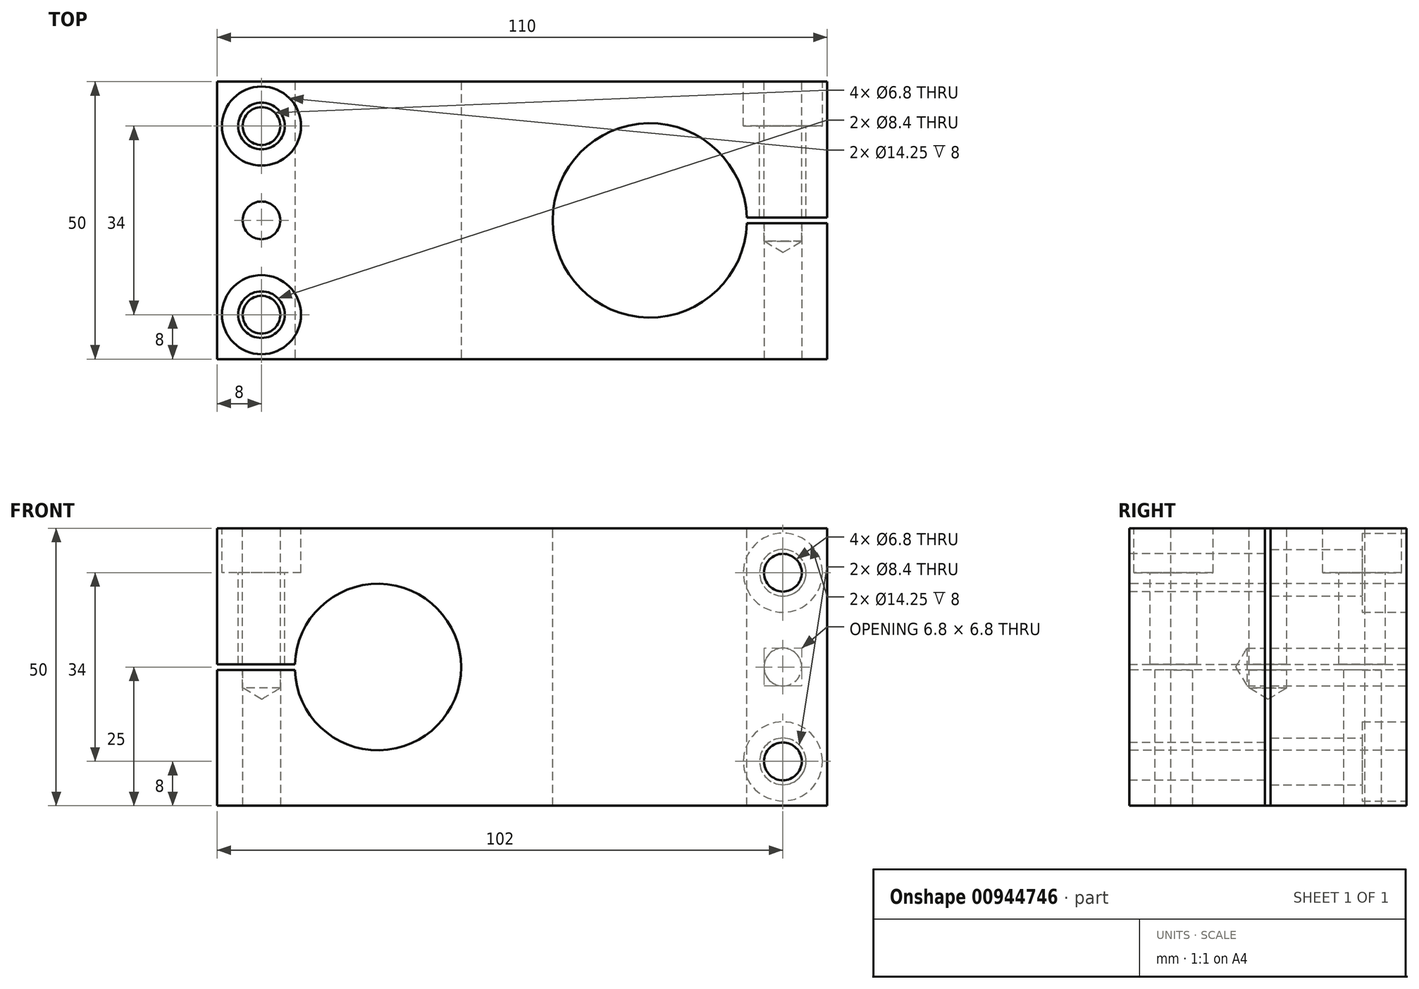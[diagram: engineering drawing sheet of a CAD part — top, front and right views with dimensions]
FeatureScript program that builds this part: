
annotation { "Feature Type Name" : "Feature", "Feature Type Description" : "" }
export const myFeature = defineFeature(function(context is Context, id is Id, definition is map)
    precondition{}
    {
        {
            var Q0;
            Q0=qCreatedBy(makeId("Top.planeOp"),FACE);
            var sketch = newSketch(context, id + "F0", { "sketchPlane" : qUnion([Q0])});
            skLineSegment(sketch, "E0.bottom", {"start": v(-55, 25) * mm, "end": v(55, 25) * mm});
            skLineSegment(sketch, "E0.top", {"start": v(-55, -25) * mm, "end": v(55, -25) * mm});
            skLineSegment(sketch, "E0.left", {"start": v(-55, 25) * mm, "end": v(-55, -25) * mm});
            skLineSegment(sketch, "E0.right", {"start": v(55, 25) * mm, "end": v(55, -25) * mm});
            skPoint(sketch, "E0.middle", {"position": v(0, 0) * mm});
            skSolve(sketch);
        }
        {
            var Q0;
            Q0 = qSketchRegion(id + "F0", true);
            extrude(context, id + "F1", {"entities" : qUnion([Q0]), "endBound" : BoundingType.SYMMETRIC, "depth" : 50 * mm, "offsetDistance" : 25 * mm});
        }
        {
            var Q0;
            Q0=makeQuery(id+"F1.opExtrude","SWEPT_FACE",FACE,{"disambiguationData":[OSD([sQuery(id+"F0.wireOp",EDGE,"E0.top")])]});
            var sketch = newSketch(context, id + "F2", { "sketchPlane" : qUnion([Q0])});
            skPoint(sketch, "E1", {"position": v(-26, 0) * mm});
            skPoint(sketch, "E2", {"position": v(47, -17) * mm});
            skPoint(sketch, "E3", {"position": v(47, 17) * mm});
            skPoint(sketch, "E4", {"position": v(47, 0) * mm});
            skSolve(sketch);
        }
        {
            var Q0;
            Q0=makeQuery(id+"F1.opExtrude","CAP_FACE",FACE,{"disambiguationData":[OSD([sQuery(id+"F0.wireOp",EDGE,"E0.bottom"),sQuery(id+"F0.wireOp",EDGE,"E0.top"),sQuery(id+"F0.wireOp",EDGE,"E0.left"),sQuery(id+"F0.wireOp",EDGE,"E0.right")])],"isStart":false});
            var sketch = newSketch(context, id + "F3", { "sketchPlane" : qUnion([Q0])});
            skPoint(sketch, "E5", {"position": v(23, 0) * mm});
            skPoint(sketch, "E6", {"position": v(-47, 17) * mm});
            skPoint(sketch, "E7", {"position": v(-47, -17) * mm});
            skPoint(sketch, "E8", {"position": v(-47, 0) * mm});
            skSolve(sketch);
        }
        {
            var Q0;
            Q0=makeQuery(id+"F1.opExtrude","CAP_FACE",FACE,{"disambiguationData":[OSD([sQuery(id+"F0.wireOp",EDGE,"E0.bottom"),sQuery(id+"F0.wireOp",EDGE,"E0.top"),sQuery(id+"F0.wireOp",EDGE,"E0.left"),sQuery(id+"F0.wireOp",EDGE,"E0.right")])],"isStart":true});
            var sketch = newSketch(context, id + "F4", { "sketchPlane" : qUnion([Q0])});
            skPoint(sketch, "E9", {"position": v(-47, -17) * mm});
            skPoint(sketch, "E10", {"position": v(-47, 17) * mm});
            skPoint(sketch, "E11", {"position": v(-47, 0) * mm});
            skSolve(sketch);
        }
        {
            var Q0;
            Q0=makeQuery(id+"F1.opExtrude","SWEPT_FACE",FACE,{"disambiguationData":[OSD([sQuery(id+"F0.wireOp",EDGE,"E0.bottom")])]});
            var sketch = newSketch(context, id + "F5", { "sketchPlane" : qUnion([Q0])});
            skPoint(sketch, "E12", {"position": v(-47, 17) * mm});
            skPoint(sketch, "E13", {"position": v(-47, -17) * mm});
            skPoint(sketch, "E14", {"position": v(-47, 0) * mm});
            skSolve(sketch);
        }
        {
            var Q0;
            Q0=sQuery(id+"F2.wireOp",VERTEX,"E1");
            var Q1;
            Q1=makeQuery(id+"F1.opExtrude","SWEPT_BODY",BODY,{"disambiguationData":[OSD([sQuery(id+"F0.wireOp",EDGE,"E0.bottom"),sQuery(id+"F0.wireOp",EDGE,"E0.top"),sQuery(id+"F0.wireOp",EDGE,"E0.left"),sQuery(id+"F0.wireOp",EDGE,"E0.right")])]});
            hole(context, id + "F6", {"style" : HoleStyle.SIMPLE, "endStyle" : HoleEndStyle.THROUGH, "holeDiameter" : 30 * mm, "majorDiameter" : 5 * mm, "isTappedThrough" : true, "tappedDepth" : 12 * mm, "tapClearance" : 3, "locations" : qUnion([Q0]), "scope" : qUnion([Q1])});
        }
        {
            var Q0;
            Q0=sQuery(id+"F3.wireOp",VERTEX,"E5");
            var Q1;
            Q1=makeQuery(id+"F1.opExtrude","SWEPT_BODY",BODY,{"disambiguationData":[OSD([sQuery(id+"F0.wireOp",EDGE,"E0.bottom"),sQuery(id+"F0.wireOp",EDGE,"E0.top"),sQuery(id+"F0.wireOp",EDGE,"E0.left"),sQuery(id+"F0.wireOp",EDGE,"E0.right")])]});
            hole(context, id + "F7", {"style" : HoleStyle.SIMPLE, "endStyle" : HoleEndStyle.THROUGH, "holeDiameter" : 35 * mm, "majorDiameter" : 5 * mm, "isTappedThrough" : true, "tappedDepth" : 12 * mm, "tapClearance" : 3, "locations" : qUnion([Q0]), "scope" : qUnion([Q1])});
        }
        {
            var Q0;
            Q0=sQuery(id+"F4.wireOp",VERTEX,"E9");
            var Q1;
            Q1=sQuery(id+"F4.wireOp",VERTEX,"E10");
            var Q2;
            Q2=sQuery(id+"F2.wireOp",VERTEX,"E3");
            var Q3;
            Q3=sQuery(id+"F2.wireOp",VERTEX,"E2");
            var Q4;
            Q4=makeQuery(id+"F1.opExtrude","SWEPT_BODY",BODY,{"disambiguationData":[OSD([sQuery(id+"F0.wireOp",EDGE,"E0.bottom"),sQuery(id+"F0.wireOp",EDGE,"E0.top"),sQuery(id+"F0.wireOp",EDGE,"E0.left"),sQuery(id+"F0.wireOp",EDGE,"E0.right")])]});
            hole(context, id + "F8", {"style" : HoleStyle.SIMPLE, "endStyle" : HoleEndStyle.BLIND, "standardTappedOrClearance" : lookupTablePath({ "standard" : "ISO", "fit" : "Normal", "engagement" : "75%", "pitch" : "1.25 mm", "size" : "M8", "type" : "Tapped" }), "standardBlindInLast" : lookupTablePath({ "fit" : "Normal", "standard" : "ISO", "engagement" : "75%", "pitch" : "1.25 mm", "size" : "M8", "type" : "Clearance & tapped" }), "holeDiameter" : 6.8 * mm, "majorDiameter" : 8 * mm, "showTappedDepth" : true, "holeDepth" : 28.25 * mm, "tappedDepth" : 24.5 * mm, "tapClearance" : 3, "startFromSketch" : true, "locations" : qUnion([Q0, Q1, Q2, Q3]), "scope" : qUnion([Q4])});
        }
        {
            var Q0;
            Q0=sQuery(id+"F3.wireOp",VERTEX,"E6");
            var Q1;
            Q1=sQuery(id+"F3.wireOp",VERTEX,"E7");
            var Q2;
            Q2=sQuery(id+"F5.wireOp",VERTEX,"E12");
            var Q3;
            Q3=sQuery(id+"F5.wireOp",VERTEX,"E13");
            var Q4;
            Q4=makeQuery(id+"F1.opExtrude","SWEPT_BODY",BODY,{"disambiguationData":[OSD([sQuery(id+"F0.wireOp",EDGE,"E0.bottom"),sQuery(id+"F0.wireOp",EDGE,"E0.top"),sQuery(id+"F0.wireOp",EDGE,"E0.left"),sQuery(id+"F0.wireOp",EDGE,"E0.right")])]});
            hole(context, id + "F9", {"style" : HoleStyle.C_BORE, "endStyle" : HoleEndStyle.BLIND, "standardTappedOrClearance" : lookupTablePath({ "standard" : "ISO", "fit" : "Close", "size" : "M8", "type" : "Clearance" }), "standardBlindInLast" : lookupTablePath({ "fit" : "Close", "standard" : "ISO", "engagement" : "75%", "pitch" : "1.25 mm", "size" : "M8", "type" : "Clearance & tapped" }), "holeDiameter" : 8.4 * mm, "cBoreDiameter" : 14.25 * mm, "cBoreDepth" : 8 * mm, "majorDiameter" : 5 * mm, "holeDepth" : 25 * mm, "isTappedThrough" : true, "tappedDepth" : 12 * mm, "tapClearance" : 3, "startFromSketch" : true, "locations" : qUnion([Q0, Q1, Q2, Q3]), "scope" : qUnion([Q4])});
        }
        {
            var Q0;
            Q0=makeQuery(id+"F1.opExtrude","SWEPT_FACE",FACE,{"disambiguationData":[OSD([sQuery(id+"F0.wireOp",EDGE,"E0.right")])]});
            var sketch = newSketch(context, id + "F10", { "sketchPlane" : qUnion([Q0])});
            skLineSegment(sketch, "E15.bottom", {"start": v(0.5, 25) * mm, "end": v(-0.5, 25) * mm});
            skLineSegment(sketch, "E15.top", {"start": v(0.5, -25) * mm, "end": v(-0.5, -25) * mm});
            skLineSegment(sketch, "E15.left", {"start": v(0.5, 25) * mm, "end": v(0.5, -25) * mm});
            skLineSegment(sketch, "E15.right", {"start": v(-0.5, 25) * mm, "end": v(-0.5, -25) * mm});
            skPoint(sketch, "E15.middle", {"position": v(0, 0) * mm});
            skSolve(sketch);
        }
        {
            var Q0;
            Q0=makeQuery(id+"F1.opExtrude","SWEPT_FACE",FACE,{"disambiguationData":[OSD([sQuery(id+"F0.wireOp",EDGE,"E0.left")])]});
            var sketch = newSketch(context, id + "F11", { "sketchPlane" : qUnion([Q0])});
            skLineSegment(sketch, "E16.bottom", {"start": v(25, -0.5) * mm, "end": v(-25, -0.5) * mm});
            skLineSegment(sketch, "E16.top", {"start": v(25, 0.5) * mm, "end": v(-25, 0.5) * mm});
            skLineSegment(sketch, "E16.left", {"start": v(25, -0.5) * mm, "end": v(25, 0.5) * mm});
            skLineSegment(sketch, "E16.right", {"start": v(-25, -0.5) * mm, "end": v(-25, 0.5) * mm});
            skPoint(sketch, "E16.middle", {"position": v(0, 0) * mm});
            skSolve(sketch);
        }
        {
            var Q0;
            Q0=makeQuery(id+"F11.imprint","IMPRINT",FACE,{"disambiguationData":[TD([[makeQuery(id+"F11.imprint","IMPRINT",EDGE,{"derivedFrom":sQuery(id+"F11.wireOp",EDGE,"E16.bottom")}),-1.0]])]});
            extrude(context, id + "F12", {"entities" : qUnion([Q0]), "operationType" : NewBodyOperationType.REMOVE, "oppositeDirection" : true, "depth" : 25 * mm, "offsetDistance" : 25 * mm});
        }
        {
            var Q0;
            Q0=makeQuery(id+"F10.imprint","IMPRINT",FACE,{"disambiguationData":[TD([[makeQuery(id+"F10.imprint","IMPRINT",EDGE,{"derivedFrom":sQuery(id+"F10.wireOp",EDGE,"E15.bottom")}),1.0]])]});
            extrude(context, id + "F13", {"entities" : qUnion([Q0]), "operationType" : NewBodyOperationType.REMOVE, "oppositeDirection" : true, "depth" : 25 * mm, "offsetDistance" : 25 * mm});
        }
        {
            var Q0;
            Q0=sQuery(id+"F5.wireOp",VERTEX,"E14");
            var Q1;
            Q1=sQuery(id+"F3.wireOp",VERTEX,"E8");
            var Q2;
            Q2=makeQuery(id+"F1.opExtrude","SWEPT_BODY",BODY,{"disambiguationData":[OSD([sQuery(id+"F0.wireOp",EDGE,"E0.bottom"),sQuery(id+"F0.wireOp",EDGE,"E0.top"),sQuery(id+"F0.wireOp",EDGE,"E0.left"),sQuery(id+"F0.wireOp",EDGE,"E0.right")])]});
            hole(context, id + "F14", {"style" : HoleStyle.SIMPLE, "endStyle" : HoleEndStyle.BLIND, "standardTappedOrClearance" : lookupTablePath({ "standard" : "ISO", "fit" : "Normal", "engagement" : "75%", "pitch" : "1.25 mm", "size" : "M8", "type" : "Tapped" }), "standardBlindInLast" : lookupTablePath({ "fit" : "Normal", "standard" : "ISO", "engagement" : "75%", "pitch" : "1.25 mm", "size" : "M8", "type" : "Clearance & tapped" }), "holeDiameter" : 6.8 * mm, "majorDiameter" : 8 * mm, "showTappedDepth" : true, "holeDepth" : 28.75 * mm, "isTappedThrough" : true, "tappedDepth" : 25 * mm, "tapClearance" : 3, "startFromSketch" : true, "locations" : qUnion([Q0, Q1]), "scope" : qUnion([Q2])});
        }
    });
